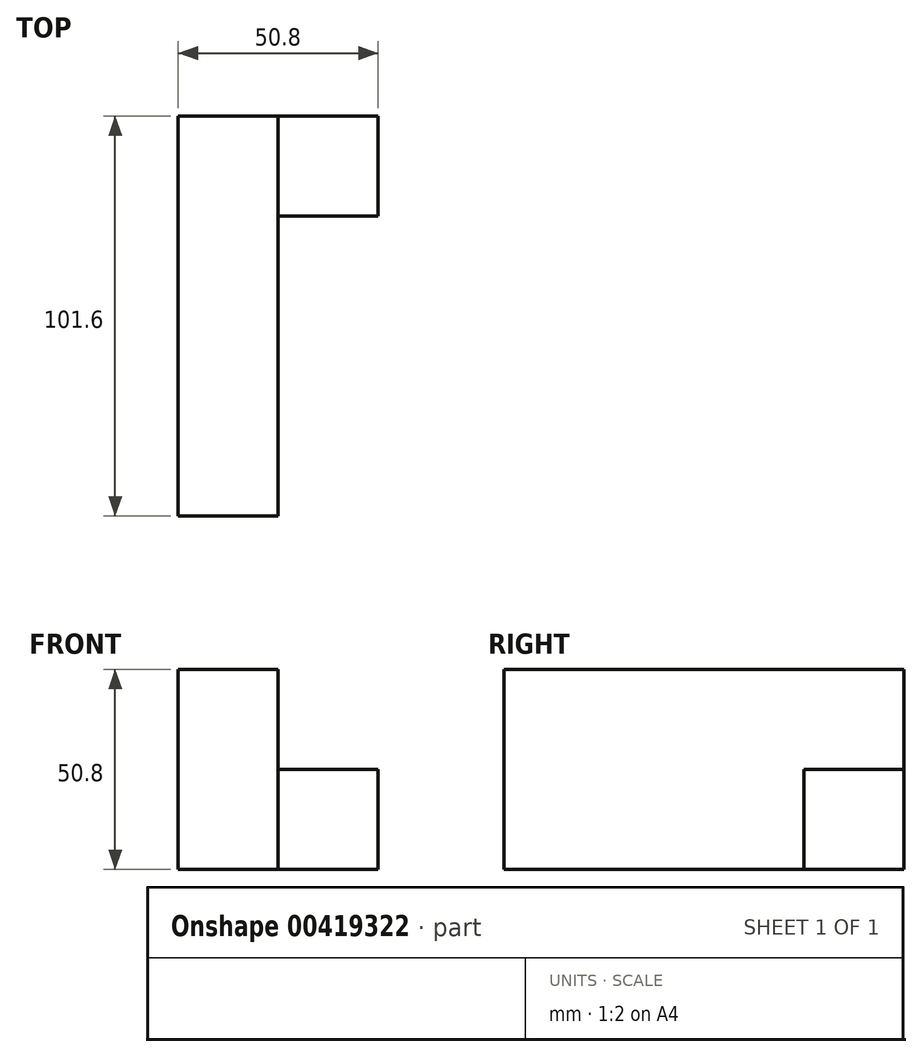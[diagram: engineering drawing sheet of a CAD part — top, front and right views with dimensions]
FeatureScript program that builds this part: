
annotation { "Feature Type Name" : "Feature", "Feature Type Description" : "" }
export const myFeature = defineFeature(function(context is Context, id is Id, definition is map)
    precondition{}
    {
        {
            var Q0;
            Q0=qCreatedBy(makeId("Front.planeOp"),FACE);
            var sketch = newSketch(context, id + "F0", { "sketchPlane" : qUnion([Q0])});
            skLineSegment(sketch, "E0", {"start": v(0, 0) * mm, "end": v(0, 50.8) * mm});
            skLineSegment(sketch, "E1", {"start": v(0, 50.8) * mm, "end": v(25.4, 50.8) * mm});
            skLineSegment(sketch, "E2", {"start": v(25.4, 50.8) * mm, "end": v(25.4, 0) * mm});
            skLineSegment(sketch, "E3", {"start": v(25.4, 0) * mm, "end": v(0, 0) * mm});
            skSolve(sketch);
        }
        {
            var Q0;
            Q0=makeQuery(id+"F0.imprint","IMPRINT",FACE,{"disambiguationData":[TD([[makeQuery(id+"F0.imprint","IMPRINT",EDGE,{"derivedFrom":sQuery(id+"F0.wireOp",EDGE,"E0")}),-1.0]])]});
            extrude(context, id + "F1", {"entities" : qUnion([Q0]), "depth" : 101.6 * mm});
        }
        {
            var Q0;
            Q0=qCreatedBy(makeId("Right.planeOp"),FACE);
            var sketch = newSketch(context, id + "F2", { "sketchPlane" : qUnion([Q0])});
            skLineSegment(sketch, "E4", {"start": v(0, 0) * mm, "end": v(-25.4, 0) * mm});
            skLineSegment(sketch, "E5", {"start": v(-25.4, 0) * mm, "end": v(-25.4, 25.4) * mm});
            skLineSegment(sketch, "E6", {"start": v(-25.4, 25.4) * mm, "end": v(0, 25.4) * mm});
            skLineSegment(sketch, "E7", {"start": v(0, 25.4) * mm, "end": v(0, 0) * mm});
            skSolve(sketch);
        }
        {
            var Q0;
            Q0=makeQuery(id+"F2.imprint","IMPRINT",FACE,{"disambiguationData":[TD([[makeQuery(id+"F2.imprint","IMPRINT",EDGE,{"derivedFrom":sQuery(id+"F2.wireOp",EDGE,"E4")}),-1.0]])]});
            extrude(context, id + "F3", {"entities" : qUnion([Q0]), "operationType" : NewBodyOperationType.ADD, "depth" : 50.8 * mm});
        }
    });
